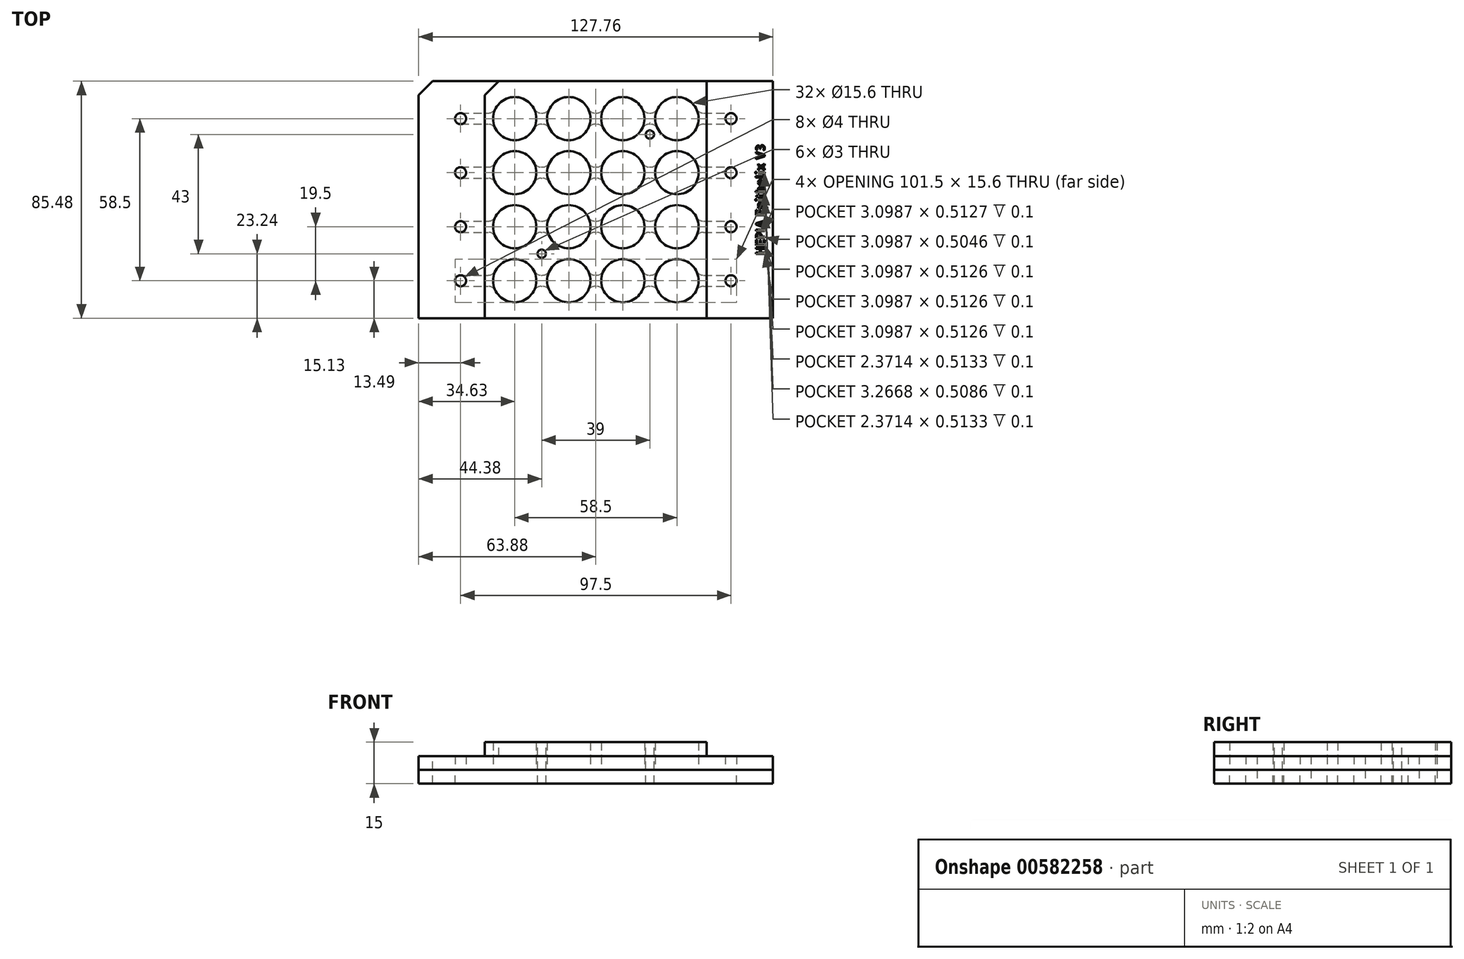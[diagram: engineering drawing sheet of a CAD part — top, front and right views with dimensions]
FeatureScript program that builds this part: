
annotation { "Feature Type Name" : "Feature", "Feature Type Description" : "" }
export const myFeature = defineFeature(function(context is Context, id is Id, definition is map)
    precondition{}
    {
        {
            var Q0;
            Q0=qCreatedBy(makeId("Top.planeOp"),FACE);
            var sketch = newSketch(context, id + "F0", { "sketchPlane" : qUnion([Q0])});
            skLineSegment(sketch, "E0.bottom", {"start": v(63.88, 42.74) * mm, "end": v(-63.88, 42.74) * mm});
            skLineSegment(sketch, "E0.top", {"start": v(63.88, -42.74) * mm, "end": v(-63.88, -42.74) * mm});
            skLineSegment(sketch, "E0.left", {"start": v(63.88, 42.74) * mm, "end": v(63.88, -42.74) * mm});
            skLineSegment(sketch, "E0.right", {"start": v(-63.88, 42.74) * mm, "end": v(-63.88, -42.74) * mm});
            skPoint(sketch, "E0.middle", {"position": v(0, 0) * mm});
            skPoint(sketch, "E1", {"position": v(-48.75, 29.25) * mm});
            skPoint(sketch, "E2.0.1.0", {"position": v(-48.75, 9.75) * mm});
            skPoint(sketch, "E2.1.0.0", {"position": v(-29.25, 29.25) * mm});
            skPoint(sketch, "E2.1.1.0", {"position": v(-29.25, 9.75) * mm});
            skPoint(sketch, "E2.2.0.0", {"position": v(-9.75, 29.25) * mm});
            skPoint(sketch, "E2.2.1.0", {"position": v(-9.75, 9.75) * mm});
            skLineSegment(sketch, "E2.direction1", {"start": v(-48.75, 29.25) * mm, "end": v(-29.25, 29.25) * mm, "construction": true});
            skLineSegment(sketch, "E2.direction2", {"start": v(-48.75, 29.25) * mm, "end": v(-48.75, 9.75) * mm, "construction": true});
            skCircle(sketch, "E3", {"center": v(-48.75, 29.25) * mm, "radius": 2 * mm});
            skCircle(sketch, "E4", {"center": v(-29.25, 29.25) * mm, "radius": 7.8 * mm});
            skCircle(sketch, "E5", {"center": v(-29.25, 9.75) * mm, "radius": 7.8 * mm});
            skCircle(sketch, "E6", {"center": v(-48.75, 9.75) * mm, "radius": 2 * mm});
            skCircle(sketch, "E7", {"center": v(-9.75, 29.25) * mm, "radius": 7.8 * mm});
            skCircle(sketch, "E8", {"center": v(-9.75, 9.75) * mm, "radius": 7.8 * mm});
            skCircle(sketch, "E9.MirrorC", {"center": v(48.75, 29.25) * mm, "radius": 2 * mm});
            skCircle(sketch, "E10.MirrorC", {"center": v(48.75, 9.75) * mm, "radius": 2 * mm});
            skCircle(sketch, "E11.MirrorC", {"center": v(29.25, 9.75) * mm, "radius": 7.8 * mm});
            skCircle(sketch, "E12.MirrorC", {"center": v(29.25, 29.25) * mm, "radius": 7.8 * mm});
            skCircle(sketch, "E13.MirrorC", {"center": v(9.75, 29.25) * mm, "radius": 7.8 * mm});
            skCircle(sketch, "E14.MirrorC", {"center": v(9.75, 9.75) * mm, "radius": 7.8 * mm});
            skCircle(sketch, "E15.MirrorC", {"center": v(-48.75, -29.25) * mm, "radius": 2 * mm});
            skCircle(sketch, "E16.MirrorC", {"center": v(-48.75, -9.75) * mm, "radius": 2 * mm});
            skCircle(sketch, "E17.MirrorC", {"center": v(-29.25, -9.75) * mm, "radius": 7.8 * mm});
            skCircle(sketch, "E18.MirrorC", {"center": v(-29.25, -29.25) * mm, "radius": 7.8 * mm});
            skCircle(sketch, "E19.MirrorC", {"center": v(-9.75, -29.25) * mm, "radius": 7.8 * mm});
            skCircle(sketch, "E20.MirrorC", {"center": v(-9.75, -9.75) * mm, "radius": 7.8 * mm});
            skCircle(sketch, "E21.MirrorC", {"center": v(9.75, -9.75) * mm, "radius": 7.8 * mm});
            skCircle(sketch, "E22.MirrorC", {"center": v(9.75, -29.25) * mm, "radius": 7.8 * mm});
            skCircle(sketch, "E23.MirrorC", {"center": v(29.25, -29.25) * mm, "radius": 7.8 * mm});
            skCircle(sketch, "E24.MirrorC", {"center": v(29.25, -9.75) * mm, "radius": 7.8 * mm});
            skCircle(sketch, "E25.MirrorC", {"center": v(48.75, -9.75) * mm, "radius": 2 * mm});
            skCircle(sketch, "E26.MirrorC", {"center": v(48.75, -29.25) * mm, "radius": 2 * mm});
            skSolve(sketch);
        }
        {
            var Q0;
            Q0 = qSketchRegion(id + "F0", true);
            extrude(context, id + "F1", {"entities" : qUnion([Q0]), "depth" : 5 * mm, "offsetDistance" : 25 * mm});
        }
        {
            var Q0;
            Q0=makeQuery(id+"F1.opExtrude","CAP_FACE",FACE,{"disambiguationData":[OSD([sQuery(id+"F0.wireOp",EDGE,"E0.bottom"),sQuery(id+"F0.wireOp",EDGE,"E0.top"),sQuery(id+"F0.wireOp",EDGE,"E0.left"),sQuery(id+"F0.wireOp",EDGE,"E0.right"),sQuery(id+"F0.wireOp",EDGE,"E3"),sQuery(id+"F0.wireOp",EDGE,"E4"),sQuery(id+"F0.wireOp",EDGE,"E5"),sQuery(id+"F0.wireOp",EDGE,"E6"),sQuery(id+"F0.wireOp",EDGE,"E7"),sQuery(id+"F0.wireOp",EDGE,"E8"),sQuery(id+"F0.wireOp",EDGE,"E9.MirrorC"),sQuery(id+"F0.wireOp",EDGE,"E10.MirrorC"),sQuery(id+"F0.wireOp",EDGE,"E11.MirrorC"),sQuery(id+"F0.wireOp",EDGE,"E12.MirrorC"),sQuery(id+"F0.wireOp",EDGE,"E13.MirrorC"),sQuery(id+"F0.wireOp",EDGE,"E14.MirrorC"),sQuery(id+"F0.wireOp",EDGE,"E15.MirrorC"),sQuery(id+"F0.wireOp",EDGE,"E16.MirrorC"),sQuery(id+"F0.wireOp",EDGE,"E17.MirrorC"),sQuery(id+"F0.wireOp",EDGE,"E18.MirrorC"),sQuery(id+"F0.wireOp",EDGE,"E19.MirrorC"),sQuery(id+"F0.wireOp",EDGE,"E20.MirrorC"),sQuery(id+"F0.wireOp",EDGE,"E21.MirrorC"),sQuery(id+"F0.wireOp",EDGE,"E22.MirrorC"),sQuery(id+"F0.wireOp",EDGE,"E23.MirrorC"),sQuery(id+"F0.wireOp",EDGE,"E24.MirrorC"),sQuery(id+"F0.wireOp",EDGE,"E25.MirrorC"),sQuery(id+"F0.wireOp",EDGE,"E26.MirrorC")])],"isStart":false});
            var sketch = newSketch(context, id + "F2", { "sketchPlane" : qUnion([Q0])});
            skLineSegment(sketch, "E27.bottom", {"start": v(40, 42.74) * mm, "end": v(-40, 42.74) * mm});
            skLineSegment(sketch, "E27.top", {"start": v(40, -42.74) * mm, "end": v(-40, -42.74) * mm});
            skLineSegment(sketch, "E27.left", {"start": v(40, 42.74) * mm, "end": v(40, -42.74) * mm});
            skLineSegment(sketch, "E27.right", {"start": v(-40, 42.74) * mm, "end": v(-40, -42.74) * mm});
            skPoint(sketch, "E27.middle", {"position": v(0, 0) * mm});
            skCircle(sketch, "E28.0", {"center": v(-29.25, -29.25) * mm, "radius": 7.8 * mm});
            skCircle(sketch, "E28.1", {"center": v(-29.25, -9.75) * mm, "radius": 7.8 * mm});
            skCircle(sketch, "E28.2", {"center": v(-29.25, 9.75) * mm, "radius": 7.8 * mm});
            skCircle(sketch, "E28.3", {"center": v(-9.75, -29.25) * mm, "radius": 7.8 * mm});
            skCircle(sketch, "E28.4", {"center": v(9.75, -29.25) * mm, "radius": 7.8 * mm});
            skCircle(sketch, "E28.5", {"center": v(9.75, -9.75) * mm, "radius": 7.8 * mm});
            skCircle(sketch, "E28.6", {"center": v(9.75, 9.75) * mm, "radius": 7.8 * mm});
            skCircle(sketch, "E28.7", {"center": v(9.75, 29.25) * mm, "radius": 7.8 * mm});
            skCircle(sketch, "E28.8", {"center": v(29.25, 29.25) * mm, "radius": 7.8 * mm});
            skCircle(sketch, "E28.9", {"center": v(29.25, 9.75) * mm, "radius": 7.8 * mm});
            skCircle(sketch, "E28.10", {"center": v(29.25, -9.75) * mm, "radius": 7.8 * mm});
            skCircle(sketch, "E28.11", {"center": v(29.25, -29.25) * mm, "radius": 7.8 * mm});
            skCircle(sketch, "E28.12", {"center": v(-29.25, 29.25) * mm, "radius": 7.8 * mm});
            skCircle(sketch, "E28.13", {"center": v(-9.75, -9.75) * mm, "radius": 7.8 * mm});
            skCircle(sketch, "E28.14", {"center": v(-9.75, 9.75) * mm, "radius": 7.8 * mm});
            skCircle(sketch, "E28.15", {"center": v(-9.75, 29.25) * mm, "radius": 7.8 * mm});
            skSolve(sketch);
        }
        {
            var Q0;
            Q0 = qSketchRegion(id + "F2", true);
            extrude(context, id + "F3", {"entities" : qUnion([Q0]), "depth" : 5 * mm, "offsetDistance" : 25 * mm});
        }
        {
            var Q0;
            Q0=makeQuery(id+"F1.opExtrude","CAP_FACE",FACE,{"disambiguationData":[OSD([sQuery(id+"F0.wireOp",EDGE,"E0.bottom"),sQuery(id+"F0.wireOp",EDGE,"E0.top"),sQuery(id+"F0.wireOp",EDGE,"E0.left"),sQuery(id+"F0.wireOp",EDGE,"E0.right"),sQuery(id+"F0.wireOp",EDGE,"E3"),sQuery(id+"F0.wireOp",EDGE,"E4"),sQuery(id+"F0.wireOp",EDGE,"E5"),sQuery(id+"F0.wireOp",EDGE,"E6"),sQuery(id+"F0.wireOp",EDGE,"E7"),sQuery(id+"F0.wireOp",EDGE,"E8"),sQuery(id+"F0.wireOp",EDGE,"E9.MirrorC"),sQuery(id+"F0.wireOp",EDGE,"E10.MirrorC"),sQuery(id+"F0.wireOp",EDGE,"E11.MirrorC"),sQuery(id+"F0.wireOp",EDGE,"E12.MirrorC"),sQuery(id+"F0.wireOp",EDGE,"E13.MirrorC"),sQuery(id+"F0.wireOp",EDGE,"E14.MirrorC"),sQuery(id+"F0.wireOp",EDGE,"E15.MirrorC"),sQuery(id+"F0.wireOp",EDGE,"E16.MirrorC"),sQuery(id+"F0.wireOp",EDGE,"E17.MirrorC"),sQuery(id+"F0.wireOp",EDGE,"E18.MirrorC"),sQuery(id+"F0.wireOp",EDGE,"E19.MirrorC"),sQuery(id+"F0.wireOp",EDGE,"E20.MirrorC"),sQuery(id+"F0.wireOp",EDGE,"E21.MirrorC"),sQuery(id+"F0.wireOp",EDGE,"E22.MirrorC"),sQuery(id+"F0.wireOp",EDGE,"E23.MirrorC"),sQuery(id+"F0.wireOp",EDGE,"E24.MirrorC"),sQuery(id+"F0.wireOp",EDGE,"E25.MirrorC"),sQuery(id+"F0.wireOp",EDGE,"E26.MirrorC")])],"isStart":true});
            var sketch = newSketch(context, id + "F4", { "sketchPlane" : qUnion([Q0])});
            skCircle(sketch, "E29.0", {"center": v(-48.75, 29.25) * mm, "radius": 2 * mm});
            skCircle(sketch, "E29.1", {"center": v(-29.25, 29.25) * mm, "radius": 7.8 * mm});
            skCircle(sketch, "E29.2", {"center": v(-9.75, 29.25) * mm, "radius": 7.8 * mm});
            skCircle(sketch, "E29.3", {"center": v(9.75, 29.25) * mm, "radius": 7.8 * mm});
            skCircle(sketch, "E29.4", {"center": v(29.25, 29.25) * mm, "radius": 7.8 * mm});
            skCircle(sketch, "E29.5", {"center": v(48.75, 29.25) * mm, "radius": 2 * mm});
            skCircle(sketch, "E29.6", {"center": v(48.75, 9.75) * mm, "radius": 2 * mm});
            skCircle(sketch, "E29.7", {"center": v(29.25, 9.75) * mm, "radius": 7.8 * mm});
            skCircle(sketch, "E29.8", {"center": v(9.75, 9.75) * mm, "radius": 7.8 * mm});
            skCircle(sketch, "E29.9", {"center": v(-9.75, 9.75) * mm, "radius": 7.8 * mm});
            skCircle(sketch, "E29.10", {"center": v(-29.25, 9.75) * mm, "radius": 7.8 * mm});
            skCircle(sketch, "E29.11", {"center": v(-48.75, 9.75) * mm, "radius": 2 * mm});
            skCircle(sketch, "E29.12", {"center": v(-48.75, -9.75) * mm, "radius": 2 * mm});
            skCircle(sketch, "E29.13", {"center": v(-29.25, -9.75) * mm, "radius": 7.8 * mm});
            skCircle(sketch, "E29.14", {"center": v(-9.75, -9.75) * mm, "radius": 7.8 * mm});
            skCircle(sketch, "E29.15", {"center": v(9.75, -9.75) * mm, "radius": 7.8 * mm});
            skCircle(sketch, "E29.16", {"center": v(29.25, -9.75) * mm, "radius": 7.8 * mm});
            skCircle(sketch, "E29.17", {"center": v(48.75, -9.75) * mm, "radius": 2 * mm});
            skCircle(sketch, "E29.18", {"center": v(48.75, -29.25) * mm, "radius": 2 * mm});
            skCircle(sketch, "E29.19", {"center": v(29.25, -29.25) * mm, "radius": 7.8 * mm});
            skCircle(sketch, "E29.20", {"center": v(9.75, -29.25) * mm, "radius": 7.8 * mm});
            skCircle(sketch, "E29.21", {"center": v(-9.75, -29.25) * mm, "radius": 7.8 * mm});
            skCircle(sketch, "E29.22", {"center": v(-29.25, -29.25) * mm, "radius": 7.8 * mm});
            skCircle(sketch, "E29.23", {"center": v(-48.75, -29.25) * mm, "radius": 2 * mm});
            skLineSegment(sketch, "E30.bottom", {"start": v(-48.75, 27.25) * mm, "end": v(48.75, 27.25) * mm});
            skLineSegment(sketch, "E30.top", {"start": v(-48.75, 31.25) * mm, "end": v(48.75, 31.25) * mm});
            skLineSegment(sketch, "E30.left", {"start": v(-48.75, 27.25) * mm, "end": v(-48.75, 31.25) * mm});
            skLineSegment(sketch, "E30.right", {"start": v(48.75, 27.25) * mm, "end": v(48.75, 31.25) * mm});
            skLineSegment(sketch, "E31.bottom", {"start": v(-48.75, 7.75) * mm, "end": v(48.75, 7.75) * mm});
            skLineSegment(sketch, "E31.top", {"start": v(-48.75, 11.75) * mm, "end": v(48.75, 11.75) * mm});
            skLineSegment(sketch, "E31.left", {"start": v(-48.75, 7.75) * mm, "end": v(-48.75, 11.75) * mm});
            skLineSegment(sketch, "E31.right", {"start": v(48.75, 7.75) * mm, "end": v(48.75, 11.75) * mm});
            skLineSegment(sketch, "E32.bottom", {"start": v(-48.75, -11.75) * mm, "end": v(48.75, -11.75) * mm});
            skLineSegment(sketch, "E32.top", {"start": v(-48.75, -7.75) * mm, "end": v(48.75, -7.75) * mm});
            skLineSegment(sketch, "E32.left", {"start": v(-48.75, -11.75) * mm, "end": v(-48.75, -7.75) * mm});
            skLineSegment(sketch, "E32.right", {"start": v(48.75, -11.75) * mm, "end": v(48.75, -7.75) * mm});
            skLineSegment(sketch, "E33.bottom", {"start": v(-48.75, -31.25) * mm, "end": v(48.75, -31.25) * mm});
            skLineSegment(sketch, "E33.top", {"start": v(-48.75, -27.25) * mm, "end": v(48.75, -27.25) * mm});
            skLineSegment(sketch, "E33.left", {"start": v(-48.75, -31.25) * mm, "end": v(-48.75, -27.25) * mm});
            skLineSegment(sketch, "E33.right", {"start": v(48.75, -31.25) * mm, "end": v(48.75, -27.25) * mm});
            skSolve(sketch);
        }
        {
            var Q0;
            Q0=makeQuery(id+"F4.imprint","IMPRINT",FACE,{"disambiguationData":[TD([[makeQuery(id+"F4.imprint","IMPRINT",EDGE,{"derivedFrom":makeQuery(id+"F1.opExtrude","CAP_EDGE",EDGE,{"disambiguationData":[OSD([sQuery(id+"F0.wireOp",EDGE,"E0.bottom")])],"isStart":true})}),-1.0]])]});
            extrude(context, id + "F5", {"entities" : qUnion([Q0]), "depth" : 5 * mm, "offsetDistance" : 25 * mm});
        }
        {
            var Q0;
            {var subQ0=sQuery(id+"F4.wireOp",EDGE,"E30.top");var subQ1=sQuery(id+"F4.wireOp",EDGE,"E29.1");Q0=makeQuery(id+"F5.opExtrude","SWEPT_EDGE",EDGE,{"disambiguationData":[OSD([subQ1,subQ0]),TDD([makeQuery(id+"F4.imprint","INTERSECT",VERTEX,{"disambiguationData":[OD(0.0)],"derivedFrom":[subQ1,subQ0]})])]});}
            var Q1;
            {var subQ0=sQuery(id+"F4.wireOp",EDGE,"E30.bottom");var subQ1=sQuery(id+"F4.wireOp",EDGE,"E29.1");Q1=makeQuery(id+"F5.opExtrude","SWEPT_EDGE",EDGE,{"disambiguationData":[OSD([subQ1,subQ0]),TDD([makeQuery(id+"F4.imprint","INTERSECT",VERTEX,{"disambiguationData":[OD(0.0)],"derivedFrom":[subQ1,subQ0]})])]});}
            var Q2;
            {var subQ0=sQuery(id+"F4.wireOp",EDGE,"E30.top");var subQ1=sQuery(id+"F4.wireOp",EDGE,"E29.1");Q2=makeQuery(id+"F5.opExtrude","SWEPT_EDGE",EDGE,{"disambiguationData":[OSD([subQ1,subQ0]),TDD([makeQuery(id+"F4.imprint","INTERSECT",VERTEX,{"disambiguationData":[OD(1.0)],"derivedFrom":[subQ1,subQ0]})])]});}
            var Q3;
            {var subQ0=sQuery(id+"F4.wireOp",EDGE,"E30.top");var subQ1=sQuery(id+"F4.wireOp",EDGE,"E29.2");Q3=makeQuery(id+"F5.opExtrude","SWEPT_EDGE",EDGE,{"disambiguationData":[OSD([subQ1,subQ0]),TDD([makeQuery(id+"F4.imprint","INTERSECT",VERTEX,{"disambiguationData":[OD(1.0)],"derivedFrom":[subQ1,subQ0]})])]});}
            var Q4;
            {var subQ0=sQuery(id+"F4.wireOp",EDGE,"E30.top");var subQ1=sQuery(id+"F4.wireOp",EDGE,"E29.3");Q4=makeQuery(id+"F5.opExtrude","SWEPT_EDGE",EDGE,{"disambiguationData":[OSD([subQ1,subQ0]),TDD([makeQuery(id+"F4.imprint","INTERSECT",VERTEX,{"disambiguationData":[OD(1.0)],"derivedFrom":[subQ1,subQ0]})])]});}
            var Q5;
            {var subQ0=sQuery(id+"F4.wireOp",EDGE,"E30.top");var subQ1=sQuery(id+"F4.wireOp",EDGE,"E29.2");Q5=makeQuery(id+"F5.opExtrude","SWEPT_EDGE",EDGE,{"disambiguationData":[OSD([subQ1,subQ0]),TDD([makeQuery(id+"F4.imprint","INTERSECT",VERTEX,{"disambiguationData":[OD(0.0)],"derivedFrom":[subQ1,subQ0]})])]});}
            var Q6;
            {var subQ0=sQuery(id+"F4.wireOp",EDGE,"E31.top");var subQ1=sQuery(id+"F4.wireOp",EDGE,"E29.10");Q6=makeQuery(id+"F5.opExtrude","SWEPT_EDGE",EDGE,{"disambiguationData":[OSD([subQ1,subQ0]),TDD([makeQuery(id+"F4.imprint","INTERSECT",VERTEX,{"disambiguationData":[OD(0.0)],"derivedFrom":[subQ1,subQ0]})])]});}
            var Q7;
            {var subQ0=sQuery(id+"F4.wireOp",EDGE,"E30.top");var subQ1=sQuery(id+"F4.wireOp",EDGE,"E29.3");Q7=makeQuery(id+"F5.opExtrude","SWEPT_EDGE",EDGE,{"disambiguationData":[OSD([subQ1,subQ0]),TDD([makeQuery(id+"F4.imprint","INTERSECT",VERTEX,{"disambiguationData":[OD(0.0)],"derivedFrom":[subQ1,subQ0]})])]});}
            var Q8;
            {var subQ0=sQuery(id+"F4.wireOp",EDGE,"E30.top");var subQ1=sQuery(id+"F4.wireOp",EDGE,"E29.4");Q8=makeQuery(id+"F5.opExtrude","SWEPT_EDGE",EDGE,{"disambiguationData":[OSD([subQ1,subQ0]),TDD([makeQuery(id+"F4.imprint","INTERSECT",VERTEX,{"disambiguationData":[OD(1.0)],"derivedFrom":[subQ1,subQ0]})])]});}
            var Q9;
            {var subQ0=sQuery(id+"F4.wireOp",EDGE,"E30.top");var subQ1=sQuery(id+"F4.wireOp",EDGE,"E29.4");Q9=makeQuery(id+"F5.opExtrude","SWEPT_EDGE",EDGE,{"disambiguationData":[OSD([subQ1,subQ0]),TDD([makeQuery(id+"F4.imprint","INTERSECT",VERTEX,{"disambiguationData":[OD(0.0)],"derivedFrom":[subQ1,subQ0]})])]});}
            var Q10;
            {var subQ0=sQuery(id+"F4.wireOp",EDGE,"E30.bottom");var subQ1=sQuery(id+"F4.wireOp",EDGE,"E29.4");Q10=makeQuery(id+"F5.opExtrude","SWEPT_EDGE",EDGE,{"disambiguationData":[OSD([subQ1,subQ0]),TDD([makeQuery(id+"F4.imprint","INTERSECT",VERTEX,{"disambiguationData":[OD(1.0)],"derivedFrom":[subQ1,subQ0]})])]});}
            var Q11;
            {var subQ0=sQuery(id+"F4.wireOp",EDGE,"E31.top");var subQ1=sQuery(id+"F4.wireOp",EDGE,"E29.10");Q11=makeQuery(id+"F5.opExtrude","SWEPT_EDGE",EDGE,{"disambiguationData":[OSD([subQ1,subQ0]),TDD([makeQuery(id+"F4.imprint","INTERSECT",VERTEX,{"disambiguationData":[OD(1.0)],"derivedFrom":[subQ1,subQ0]})])]});}
            var Q12;
            {var subQ0=sQuery(id+"F4.wireOp",EDGE,"E31.top");var subQ1=sQuery(id+"F4.wireOp",EDGE,"E29.9");Q12=makeQuery(id+"F5.opExtrude","SWEPT_EDGE",EDGE,{"disambiguationData":[OSD([subQ1,subQ0]),TDD([makeQuery(id+"F4.imprint","INTERSECT",VERTEX,{"disambiguationData":[OD(0.0)],"derivedFrom":[subQ1,subQ0]})])]});}
            var Q13;
            {var subQ0=sQuery(id+"F4.wireOp",EDGE,"E31.top");var subQ1=sQuery(id+"F4.wireOp",EDGE,"E29.9");Q13=makeQuery(id+"F5.opExtrude","SWEPT_EDGE",EDGE,{"disambiguationData":[OSD([subQ1,subQ0]),TDD([makeQuery(id+"F4.imprint","INTERSECT",VERTEX,{"disambiguationData":[OD(1.0)],"derivedFrom":[subQ1,subQ0]})])]});}
            var Q14;
            {var subQ0=sQuery(id+"F4.wireOp",EDGE,"E31.top");var subQ1=sQuery(id+"F4.wireOp",EDGE,"E29.8");Q14=makeQuery(id+"F5.opExtrude","SWEPT_EDGE",EDGE,{"disambiguationData":[OSD([subQ1,subQ0]),TDD([makeQuery(id+"F4.imprint","INTERSECT",VERTEX,{"disambiguationData":[OD(1.0)],"derivedFrom":[subQ1,subQ0]})])]});}
            var Q15;
            {var subQ0=sQuery(id+"F4.wireOp",EDGE,"E31.top");var subQ1=sQuery(id+"F4.wireOp",EDGE,"E29.8");Q15=makeQuery(id+"F5.opExtrude","SWEPT_EDGE",EDGE,{"disambiguationData":[OSD([subQ1,subQ0]),TDD([makeQuery(id+"F4.imprint","INTERSECT",VERTEX,{"disambiguationData":[OD(0.0)],"derivedFrom":[subQ1,subQ0]})])]});}
            var Q16;
            {var subQ0=sQuery(id+"F4.wireOp",EDGE,"E31.top");var subQ1=sQuery(id+"F4.wireOp",EDGE,"E29.7");Q16=makeQuery(id+"F5.opExtrude","SWEPT_EDGE",EDGE,{"disambiguationData":[OSD([subQ1,subQ0]),TDD([makeQuery(id+"F4.imprint","INTERSECT",VERTEX,{"disambiguationData":[OD(1.0)],"derivedFrom":[subQ1,subQ0]})])]});}
            var Q17;
            {var subQ0=sQuery(id+"F4.wireOp",EDGE,"E31.top");var subQ1=sQuery(id+"F4.wireOp",EDGE,"E29.7");Q17=makeQuery(id+"F5.opExtrude","SWEPT_EDGE",EDGE,{"disambiguationData":[OSD([subQ1,subQ0]),TDD([makeQuery(id+"F4.imprint","INTERSECT",VERTEX,{"disambiguationData":[OD(0.0)],"derivedFrom":[subQ1,subQ0]})])]});}
            var Q18;
            {var subQ0=sQuery(id+"F4.wireOp",EDGE,"E32.top");var subQ1=sQuery(id+"F4.wireOp",EDGE,"E29.16");Q18=makeQuery(id+"F5.opExtrude","SWEPT_EDGE",EDGE,{"disambiguationData":[OSD([subQ1,subQ0]),TDD([makeQuery(id+"F4.imprint","INTERSECT",VERTEX,{"disambiguationData":[OD(0.0)],"derivedFrom":[subQ1,subQ0]})])]});}
            var Q19;
            {var subQ0=sQuery(id+"F4.wireOp",EDGE,"E33.top");var subQ1=sQuery(id+"F4.wireOp",EDGE,"E29.19");Q19=makeQuery(id+"F5.opExtrude","SWEPT_EDGE",EDGE,{"disambiguationData":[OSD([subQ1,subQ0]),TDD([makeQuery(id+"F4.imprint","INTERSECT",VERTEX,{"disambiguationData":[OD(0.0)],"derivedFrom":[subQ1,subQ0]})])]});}
            var Q20;
            {var subQ0=sQuery(id+"F4.wireOp",EDGE,"E33.top");var subQ1=sQuery(id+"F4.wireOp",EDGE,"E29.19");Q20=makeQuery(id+"F5.opExtrude","SWEPT_EDGE",EDGE,{"disambiguationData":[OSD([subQ1,subQ0]),TDD([makeQuery(id+"F4.imprint","INTERSECT",VERTEX,{"disambiguationData":[OD(1.0)],"derivedFrom":[subQ1,subQ0]})])]});}
            var Q21;
            {var subQ0=sQuery(id+"F4.wireOp",EDGE,"E32.top");var subQ1=sQuery(id+"F4.wireOp",EDGE,"E29.16");Q21=makeQuery(id+"F5.opExtrude","SWEPT_EDGE",EDGE,{"disambiguationData":[OSD([subQ1,subQ0]),TDD([makeQuery(id+"F4.imprint","INTERSECT",VERTEX,{"disambiguationData":[OD(1.0)],"derivedFrom":[subQ1,subQ0]})])]});}
            var Q22;
            {var subQ0=sQuery(id+"F4.wireOp",EDGE,"E32.top");var subQ1=sQuery(id+"F4.wireOp",EDGE,"E29.15");Q22=makeQuery(id+"F5.opExtrude","SWEPT_EDGE",EDGE,{"disambiguationData":[OSD([subQ1,subQ0]),TDD([makeQuery(id+"F4.imprint","INTERSECT",VERTEX,{"disambiguationData":[OD(0.0)],"derivedFrom":[subQ1,subQ0]})])]});}
            var Q23;
            {var subQ0=sQuery(id+"F4.wireOp",EDGE,"E32.bottom");var subQ1=sQuery(id+"F4.wireOp",EDGE,"E29.16");Q23=makeQuery(id+"F5.opExtrude","SWEPT_EDGE",EDGE,{"disambiguationData":[OSD([subQ1,subQ0]),TDD([makeQuery(id+"F4.imprint","INTERSECT",VERTEX,{"disambiguationData":[OD(1.0)],"derivedFrom":[subQ1,subQ0]})])]});}
            var Q24;
            {var subQ0=sQuery(id+"F4.wireOp",EDGE,"E31.bottom");var subQ1=sQuery(id+"F4.wireOp",EDGE,"E29.7");Q24=makeQuery(id+"F5.opExtrude","SWEPT_EDGE",EDGE,{"disambiguationData":[OSD([subQ1,subQ0]),TDD([makeQuery(id+"F4.imprint","INTERSECT",VERTEX,{"disambiguationData":[OD(1.0)],"derivedFrom":[subQ1,subQ0]})])]});}
            var Q25;
            {var subQ0=sQuery(id+"F4.wireOp",EDGE,"E30.bottom");var subQ1=sQuery(id+"F4.wireOp",EDGE,"E29.3");Q25=makeQuery(id+"F5.opExtrude","SWEPT_EDGE",EDGE,{"disambiguationData":[OSD([subQ1,subQ0]),TDD([makeQuery(id+"F4.imprint","INTERSECT",VERTEX,{"disambiguationData":[OD(1.0)],"derivedFrom":[subQ1,subQ0]})])]});}
            var Q26;
            {var subQ0=sQuery(id+"F4.wireOp",EDGE,"E30.bottom");var subQ1=sQuery(id+"F4.wireOp",EDGE,"E29.2");Q26=makeQuery(id+"F5.opExtrude","SWEPT_EDGE",EDGE,{"disambiguationData":[OSD([subQ1,subQ0]),TDD([makeQuery(id+"F4.imprint","INTERSECT",VERTEX,{"disambiguationData":[OD(0.0)],"derivedFrom":[subQ1,subQ0]})])]});}
            var Q27;
            {var subQ0=sQuery(id+"F4.wireOp",EDGE,"E31.bottom");var subQ1=sQuery(id+"F4.wireOp",EDGE,"E29.9");Q27=makeQuery(id+"F5.opExtrude","SWEPT_EDGE",EDGE,{"disambiguationData":[OSD([subQ1,subQ0]),TDD([makeQuery(id+"F4.imprint","INTERSECT",VERTEX,{"disambiguationData":[OD(0.0)],"derivedFrom":[subQ1,subQ0]})])]});}
            var Q28;
            {var subQ0=sQuery(id+"F4.wireOp",EDGE,"E31.bottom");var subQ1=sQuery(id+"F4.wireOp",EDGE,"E29.8");Q28=makeQuery(id+"F5.opExtrude","SWEPT_EDGE",EDGE,{"disambiguationData":[OSD([subQ1,subQ0]),TDD([makeQuery(id+"F4.imprint","INTERSECT",VERTEX,{"disambiguationData":[OD(1.0)],"derivedFrom":[subQ1,subQ0]})])]});}
            var Q29;
            {var subQ0=sQuery(id+"F4.wireOp",EDGE,"E32.top");var subQ1=sQuery(id+"F4.wireOp",EDGE,"E29.13");Q29=makeQuery(id+"F5.opExtrude","SWEPT_EDGE",EDGE,{"disambiguationData":[OSD([subQ1,subQ0]),TDD([makeQuery(id+"F4.imprint","INTERSECT",VERTEX,{"disambiguationData":[OD(0.0)],"derivedFrom":[subQ1,subQ0]})])]});}
            var Q30;
            {var subQ0=sQuery(id+"F4.wireOp",EDGE,"E32.top");var subQ1=sQuery(id+"F4.wireOp",EDGE,"E29.13");Q30=makeQuery(id+"F5.opExtrude","SWEPT_EDGE",EDGE,{"disambiguationData":[OSD([subQ1,subQ0]),TDD([makeQuery(id+"F4.imprint","INTERSECT",VERTEX,{"disambiguationData":[OD(1.0)],"derivedFrom":[subQ1,subQ0]})])]});}
            var Q31;
            {var subQ0=sQuery(id+"F4.wireOp",EDGE,"E32.bottom");var subQ1=sQuery(id+"F4.wireOp",EDGE,"E29.13");Q31=makeQuery(id+"F5.opExtrude","SWEPT_EDGE",EDGE,{"disambiguationData":[OSD([subQ1,subQ0]),TDD([makeQuery(id+"F4.imprint","INTERSECT",VERTEX,{"disambiguationData":[OD(0.0)],"derivedFrom":[subQ1,subQ0]})])]});}
            var Q32;
            {var subQ0=sQuery(id+"F4.wireOp",EDGE,"E32.top");var subQ1=sQuery(id+"F4.wireOp",EDGE,"E29.14");Q32=makeQuery(id+"F5.opExtrude","SWEPT_EDGE",EDGE,{"disambiguationData":[OSD([subQ1,subQ0]),TDD([makeQuery(id+"F4.imprint","INTERSECT",VERTEX,{"disambiguationData":[OD(0.0)],"derivedFrom":[subQ1,subQ0]})])]});}
            var Q33;
            {var subQ0=sQuery(id+"F4.wireOp",EDGE,"E32.bottom");var subQ1=sQuery(id+"F4.wireOp",EDGE,"E29.14");Q33=makeQuery(id+"F5.opExtrude","SWEPT_EDGE",EDGE,{"disambiguationData":[OSD([subQ1,subQ0]),TDD([makeQuery(id+"F4.imprint","INTERSECT",VERTEX,{"disambiguationData":[OD(0.0)],"derivedFrom":[subQ1,subQ0]})])]});}
            var Q34;
            {var subQ0=sQuery(id+"F4.wireOp",EDGE,"E32.top");var subQ1=sQuery(id+"F4.wireOp",EDGE,"E29.14");Q34=makeQuery(id+"F5.opExtrude","SWEPT_EDGE",EDGE,{"disambiguationData":[OSD([subQ1,subQ0]),TDD([makeQuery(id+"F4.imprint","INTERSECT",VERTEX,{"disambiguationData":[OD(1.0)],"derivedFrom":[subQ1,subQ0]})])]});}
            var Q35;
            {var subQ0=sQuery(id+"F4.wireOp",EDGE,"E32.top");var subQ1=sQuery(id+"F4.wireOp",EDGE,"E29.15");Q35=makeQuery(id+"F5.opExtrude","SWEPT_EDGE",EDGE,{"disambiguationData":[OSD([subQ1,subQ0]),TDD([makeQuery(id+"F4.imprint","INTERSECT",VERTEX,{"disambiguationData":[OD(1.0)],"derivedFrom":[subQ1,subQ0]})])]});}
            var Q36;
            {var subQ0=sQuery(id+"F4.wireOp",EDGE,"E32.bottom");var subQ1=sQuery(id+"F4.wireOp",EDGE,"E29.15");Q36=makeQuery(id+"F5.opExtrude","SWEPT_EDGE",EDGE,{"disambiguationData":[OSD([subQ1,subQ0]),TDD([makeQuery(id+"F4.imprint","INTERSECT",VERTEX,{"disambiguationData":[OD(1.0)],"derivedFrom":[subQ1,subQ0]})])]});}
            var Q37;
            {var subQ0=sQuery(id+"F4.wireOp",EDGE,"E33.top");var subQ1=sQuery(id+"F4.wireOp",EDGE,"E29.22");Q37=makeQuery(id+"F5.opExtrude","SWEPT_EDGE",EDGE,{"disambiguationData":[OSD([subQ1,subQ0]),TDD([makeQuery(id+"F4.imprint","INTERSECT",VERTEX,{"disambiguationData":[OD(0.0)],"derivedFrom":[subQ1,subQ0]})])]});}
            var Q38;
            {var subQ0=sQuery(id+"F4.wireOp",EDGE,"E33.bottom");var subQ1=sQuery(id+"F4.wireOp",EDGE,"E29.22");Q38=makeQuery(id+"F5.opExtrude","SWEPT_EDGE",EDGE,{"disambiguationData":[OSD([subQ1,subQ0]),TDD([makeQuery(id+"F4.imprint","INTERSECT",VERTEX,{"disambiguationData":[OD(0.0)],"derivedFrom":[subQ1,subQ0]})])]});}
            var Q39;
            {var subQ0=sQuery(id+"F4.wireOp",EDGE,"E33.top");var subQ1=sQuery(id+"F4.wireOp",EDGE,"E29.22");Q39=makeQuery(id+"F5.opExtrude","SWEPT_EDGE",EDGE,{"disambiguationData":[OSD([subQ1,subQ0]),TDD([makeQuery(id+"F4.imprint","INTERSECT",VERTEX,{"disambiguationData":[OD(1.0)],"derivedFrom":[subQ1,subQ0]})])]});}
            var Q40;
            {var subQ0=sQuery(id+"F4.wireOp",EDGE,"E33.top");var subQ1=sQuery(id+"F4.wireOp",EDGE,"E29.21");Q40=makeQuery(id+"F5.opExtrude","SWEPT_EDGE",EDGE,{"disambiguationData":[OSD([subQ1,subQ0]),TDD([makeQuery(id+"F4.imprint","INTERSECT",VERTEX,{"disambiguationData":[OD(0.0)],"derivedFrom":[subQ1,subQ0]})])]});}
            var Q41;
            {var subQ0=sQuery(id+"F4.wireOp",EDGE,"E33.bottom");var subQ1=sQuery(id+"F4.wireOp",EDGE,"E29.21");Q41=makeQuery(id+"F5.opExtrude","SWEPT_EDGE",EDGE,{"disambiguationData":[OSD([subQ1,subQ0]),TDD([makeQuery(id+"F4.imprint","INTERSECT",VERTEX,{"disambiguationData":[OD(0.0)],"derivedFrom":[subQ1,subQ0]})])]});}
            var Q42;
            {var subQ0=sQuery(id+"F4.wireOp",EDGE,"E33.top");var subQ1=sQuery(id+"F4.wireOp",EDGE,"E29.21");Q42=makeQuery(id+"F5.opExtrude","SWEPT_EDGE",EDGE,{"disambiguationData":[OSD([subQ1,subQ0]),TDD([makeQuery(id+"F4.imprint","INTERSECT",VERTEX,{"disambiguationData":[OD(1.0)],"derivedFrom":[subQ1,subQ0]})])]});}
            var Q43;
            {var subQ0=sQuery(id+"F4.wireOp",EDGE,"E33.top");var subQ1=sQuery(id+"F4.wireOp",EDGE,"E29.20");Q43=makeQuery(id+"F5.opExtrude","SWEPT_EDGE",EDGE,{"disambiguationData":[OSD([subQ1,subQ0]),TDD([makeQuery(id+"F4.imprint","INTERSECT",VERTEX,{"disambiguationData":[OD(1.0)],"derivedFrom":[subQ1,subQ0]})])]});}
            var Q44;
            {var subQ0=sQuery(id+"F4.wireOp",EDGE,"E33.bottom");var subQ1=sQuery(id+"F4.wireOp",EDGE,"E29.20");Q44=makeQuery(id+"F5.opExtrude","SWEPT_EDGE",EDGE,{"disambiguationData":[OSD([subQ1,subQ0]),TDD([makeQuery(id+"F4.imprint","INTERSECT",VERTEX,{"disambiguationData":[OD(1.0)],"derivedFrom":[subQ1,subQ0]})])]});}
            var Q45;
            {var subQ0=sQuery(id+"F4.wireOp",EDGE,"E33.top");var subQ1=sQuery(id+"F4.wireOp",EDGE,"E29.20");Q45=makeQuery(id+"F5.opExtrude","SWEPT_EDGE",EDGE,{"disambiguationData":[OSD([subQ1,subQ0]),TDD([makeQuery(id+"F4.imprint","INTERSECT",VERTEX,{"disambiguationData":[OD(0.0)],"derivedFrom":[subQ1,subQ0]})])]});}
            var Q46;
            {var subQ0=sQuery(id+"F4.wireOp",EDGE,"E33.bottom");var subQ1=sQuery(id+"F4.wireOp",EDGE,"E29.19");Q46=makeQuery(id+"F5.opExtrude","SWEPT_EDGE",EDGE,{"disambiguationData":[OSD([subQ1,subQ0]),TDD([makeQuery(id+"F4.imprint","INTERSECT",VERTEX,{"disambiguationData":[OD(1.0)],"derivedFrom":[subQ1,subQ0]})])]});}
            var Q47;
            {var subQ0=sQuery(id+"F4.wireOp",EDGE,"E30.bottom");var subQ1=sQuery(id+"F4.wireOp",EDGE,"E29.1");Q47=makeQuery(id+"F5.opExtrude","SWEPT_EDGE",EDGE,{"disambiguationData":[OSD([subQ1,subQ0]),TDD([makeQuery(id+"F4.imprint","INTERSECT",VERTEX,{"disambiguationData":[OD(1.0)],"derivedFrom":[subQ1,subQ0]})])]});}
            var Q48;
            {var subQ0=sQuery(id+"F4.wireOp",EDGE,"E30.bottom");var subQ1=sQuery(id+"F4.wireOp",EDGE,"E29.2");Q48=makeQuery(id+"F5.opExtrude","SWEPT_EDGE",EDGE,{"disambiguationData":[OSD([subQ1,subQ0]),TDD([makeQuery(id+"F4.imprint","INTERSECT",VERTEX,{"disambiguationData":[OD(1.0)],"derivedFrom":[subQ1,subQ0]})])]});}
            var Q49;
            {var subQ0=sQuery(id+"F4.wireOp",EDGE,"E30.bottom");var subQ1=sQuery(id+"F4.wireOp",EDGE,"E29.3");Q49=makeQuery(id+"F5.opExtrude","SWEPT_EDGE",EDGE,{"disambiguationData":[OSD([subQ1,subQ0]),TDD([makeQuery(id+"F4.imprint","INTERSECT",VERTEX,{"disambiguationData":[OD(0.0)],"derivedFrom":[subQ1,subQ0]})])]});}
            var Q50;
            {var subQ0=sQuery(id+"F4.wireOp",EDGE,"E30.bottom");var subQ1=sQuery(id+"F4.wireOp",EDGE,"E29.4");Q50=makeQuery(id+"F5.opExtrude","SWEPT_EDGE",EDGE,{"disambiguationData":[OSD([subQ1,subQ0]),TDD([makeQuery(id+"F4.imprint","INTERSECT",VERTEX,{"disambiguationData":[OD(0.0)],"derivedFrom":[subQ1,subQ0]})])]});}
            var Q51;
            {var subQ0=sQuery(id+"F4.wireOp",EDGE,"E31.bottom");var subQ1=sQuery(id+"F4.wireOp",EDGE,"E29.7");Q51=makeQuery(id+"F5.opExtrude","SWEPT_EDGE",EDGE,{"disambiguationData":[OSD([subQ1,subQ0]),TDD([makeQuery(id+"F4.imprint","INTERSECT",VERTEX,{"disambiguationData":[OD(0.0)],"derivedFrom":[subQ1,subQ0]})])]});}
            var Q52;
            {var subQ0=sQuery(id+"F4.wireOp",EDGE,"E32.bottom");var subQ1=sQuery(id+"F4.wireOp",EDGE,"E29.16");Q52=makeQuery(id+"F5.opExtrude","SWEPT_EDGE",EDGE,{"disambiguationData":[OSD([subQ1,subQ0]),TDD([makeQuery(id+"F4.imprint","INTERSECT",VERTEX,{"disambiguationData":[OD(0.0)],"derivedFrom":[subQ1,subQ0]})])]});}
            var Q53;
            {var subQ0=sQuery(id+"F4.wireOp",EDGE,"E33.bottom");var subQ1=sQuery(id+"F4.wireOp",EDGE,"E29.19");Q53=makeQuery(id+"F5.opExtrude","SWEPT_EDGE",EDGE,{"disambiguationData":[OSD([subQ1,subQ0]),TDD([makeQuery(id+"F4.imprint","INTERSECT",VERTEX,{"disambiguationData":[OD(0.0)],"derivedFrom":[subQ1,subQ0]})])]});}
            var Q54;
            {var subQ0=sQuery(id+"F4.wireOp",EDGE,"E33.bottom");var subQ1=sQuery(id+"F4.wireOp",EDGE,"E29.20");Q54=makeQuery(id+"F5.opExtrude","SWEPT_EDGE",EDGE,{"disambiguationData":[OSD([subQ1,subQ0]),TDD([makeQuery(id+"F4.imprint","INTERSECT",VERTEX,{"disambiguationData":[OD(0.0)],"derivedFrom":[subQ1,subQ0]})])]});}
            var Q55;
            {var subQ0=sQuery(id+"F4.wireOp",EDGE,"E32.bottom");var subQ1=sQuery(id+"F4.wireOp",EDGE,"E29.15");Q55=makeQuery(id+"F5.opExtrude","SWEPT_EDGE",EDGE,{"disambiguationData":[OSD([subQ1,subQ0]),TDD([makeQuery(id+"F4.imprint","INTERSECT",VERTEX,{"disambiguationData":[OD(0.0)],"derivedFrom":[subQ1,subQ0]})])]});}
            var Q56;
            {var subQ0=sQuery(id+"F4.wireOp",EDGE,"E31.bottom");var subQ1=sQuery(id+"F4.wireOp",EDGE,"E29.8");Q56=makeQuery(id+"F5.opExtrude","SWEPT_EDGE",EDGE,{"disambiguationData":[OSD([subQ1,subQ0]),TDD([makeQuery(id+"F4.imprint","INTERSECT",VERTEX,{"disambiguationData":[OD(0.0)],"derivedFrom":[subQ1,subQ0]})])]});}
            var Q57;
            {var subQ0=sQuery(id+"F4.wireOp",EDGE,"E31.bottom");var subQ1=sQuery(id+"F4.wireOp",EDGE,"E29.9");Q57=makeQuery(id+"F5.opExtrude","SWEPT_EDGE",EDGE,{"disambiguationData":[OSD([subQ1,subQ0]),TDD([makeQuery(id+"F4.imprint","INTERSECT",VERTEX,{"disambiguationData":[OD(1.0)],"derivedFrom":[subQ1,subQ0]})])]});}
            var Q58;
            {var subQ0=sQuery(id+"F4.wireOp",EDGE,"E32.bottom");var subQ1=sQuery(id+"F4.wireOp",EDGE,"E29.14");Q58=makeQuery(id+"F5.opExtrude","SWEPT_EDGE",EDGE,{"disambiguationData":[OSD([subQ1,subQ0]),TDD([makeQuery(id+"F4.imprint","INTERSECT",VERTEX,{"disambiguationData":[OD(1.0)],"derivedFrom":[subQ1,subQ0]})])]});}
            var Q59;
            {var subQ0=sQuery(id+"F4.wireOp",EDGE,"E33.bottom");var subQ1=sQuery(id+"F4.wireOp",EDGE,"E29.21");Q59=makeQuery(id+"F5.opExtrude","SWEPT_EDGE",EDGE,{"disambiguationData":[OSD([subQ1,subQ0]),TDD([makeQuery(id+"F4.imprint","INTERSECT",VERTEX,{"disambiguationData":[OD(1.0)],"derivedFrom":[subQ1,subQ0]})])]});}
            var Q60;
            {var subQ0=sQuery(id+"F4.wireOp",EDGE,"E33.bottom");var subQ1=sQuery(id+"F4.wireOp",EDGE,"E29.22");Q60=makeQuery(id+"F5.opExtrude","SWEPT_EDGE",EDGE,{"disambiguationData":[OSD([subQ1,subQ0]),TDD([makeQuery(id+"F4.imprint","INTERSECT",VERTEX,{"disambiguationData":[OD(1.0)],"derivedFrom":[subQ1,subQ0]})])]});}
            var Q61;
            {var subQ0=sQuery(id+"F4.wireOp",EDGE,"E32.bottom");var subQ1=sQuery(id+"F4.wireOp",EDGE,"E29.13");Q61=makeQuery(id+"F5.opExtrude","SWEPT_EDGE",EDGE,{"disambiguationData":[OSD([subQ1,subQ0]),TDD([makeQuery(id+"F4.imprint","INTERSECT",VERTEX,{"disambiguationData":[OD(1.0)],"derivedFrom":[subQ1,subQ0]})])]});}
            var Q62;
            {var subQ0=sQuery(id+"F4.wireOp",EDGE,"E31.bottom");var subQ1=sQuery(id+"F4.wireOp",EDGE,"E29.10");Q62=makeQuery(id+"F5.opExtrude","SWEPT_EDGE",EDGE,{"disambiguationData":[OSD([subQ1,subQ0]),TDD([makeQuery(id+"F4.imprint","INTERSECT",VERTEX,{"disambiguationData":[OD(1.0)],"derivedFrom":[subQ1,subQ0]})])]});}
            var Q63;
            {var subQ0=sQuery(id+"F4.wireOp",EDGE,"E31.bottom");var subQ1=sQuery(id+"F4.wireOp",EDGE,"E29.10");Q63=makeQuery(id+"F5.opExtrude","SWEPT_EDGE",EDGE,{"disambiguationData":[OSD([subQ1,subQ0]),TDD([makeQuery(id+"F4.imprint","INTERSECT",VERTEX,{"disambiguationData":[OD(0.0)],"derivedFrom":[subQ1,subQ0]})])]});}
            fillet(context, id + "F6", {"entities" : qUnion([Q0, Q1, Q2, Q3, Q4, Q5, Q6, Q7, Q8, Q9, Q10, Q11, Q12, Q13, Q14, Q15, Q16, Q17, Q18, Q19, Q20, Q21, Q22, Q23, Q24, Q25, Q26, Q27, Q28, Q29, Q30, Q31, Q32, Q33, Q34, Q35, Q36, Q37, Q38, Q39, Q40, Q41, Q42, Q43, Q44, Q45, Q46, Q47, Q48, Q49, Q50, Q51, Q52, Q53, Q54, Q55, Q56, Q57, Q58, Q59, Q60, Q61, Q62, Q63]), "radius" : 3 * mm, "tangentPropagation" : true, "allowEdgeOverflow" : false});
        }
        {
            var Q0;
            Q0=makeQuery(id+"F3.opExtrude","CAP_FACE",FACE,{"disambiguationData":[OSD([sQuery(id+"F2.wireOp",EDGE,"E27.bottom"),sQuery(id+"F2.wireOp",EDGE,"E27.top"),sQuery(id+"F2.wireOp",EDGE,"E27.left"),sQuery(id+"F2.wireOp",EDGE,"E27.right"),sQuery(id+"F2.wireOp",EDGE,"E28.0"),sQuery(id+"F2.wireOp",EDGE,"E28.1"),sQuery(id+"F2.wireOp",EDGE,"E28.2"),sQuery(id+"F2.wireOp",EDGE,"E28.3"),sQuery(id+"F2.wireOp",EDGE,"E28.4"),sQuery(id+"F2.wireOp",EDGE,"E28.5"),sQuery(id+"F2.wireOp",EDGE,"E28.6"),sQuery(id+"F2.wireOp",EDGE,"E28.7"),sQuery(id+"F2.wireOp",EDGE,"E28.8"),sQuery(id+"F2.wireOp",EDGE,"E28.9"),sQuery(id+"F2.wireOp",EDGE,"E28.10"),sQuery(id+"F2.wireOp",EDGE,"E28.11"),sQuery(id+"F2.wireOp",EDGE,"E28.12"),sQuery(id+"F2.wireOp",EDGE,"E28.13"),sQuery(id+"F2.wireOp",EDGE,"E28.14"),sQuery(id+"F2.wireOp",EDGE,"E28.15")])],"isStart":false});
            var sketch = newSketch(context, id + "F7", { "sketchPlane" : qUnion([Q0])});
            skCircle(sketch, "E34", {"center": v(-19.5, -19.5) * mm, "radius": 1.5 * mm});
            skCircle(sketch, "E35", {"center": v(19.5, 23.5) * mm, "radius": 1.5 * mm});
            skPoint(sketch, "E36", {"position": v(-29.25, -29.25) * mm});
            skPoint(sketch, "E37", {"position": v(-9.75, -9.75) * mm});
            skLineSegment(sketch, "E38", {"start": v(29.25, 29.25) * mm, "end": v(9.75, 9.75) * mm, "construction": true});
            skPoint(sketch, "E39", {"position": v(19.5, 19.5) * mm});
            skSolve(sketch);
        }
        {
            var Q0;
            Q0 = qSketchRegion(id + "F7", true);
            extrude(context, id + "F8", {"entities" : qUnion([Q0]), "operationType" : NewBodyOperationType.REMOVE, "endBound" : BoundingType.THROUGH_ALL, "oppositeDirection" : true, "depth" : 25 * mm, "offsetDistance" : 25 * mm});
        }
        {
            var Q0;
            Q0=makeQuery(id+"F3.opExtrude","SWEPT_EDGE",EDGE,{"disambiguationData":[OSD([sQuery(id+"F0.wireOp",EDGE,"E0.bottom"),sQuery(id+"F2.wireOp",EDGE,"E27.bottom"),sQuery(id+"F2.wireOp",EDGE,"E27.right")])]});
            var Q1;
            Q1=makeQuery(id+"F5.opExtrude","SWEPT_EDGE",EDGE,{"disambiguationData":[OSD([sQuery(id+"F0.wireOp",EDGE,"E0.bottom"),sQuery(id+"F0.wireOp",EDGE,"E0.right")])]});
            var Q2;
            Q2=makeQuery(id+"F1.opExtrude","SWEPT_EDGE",EDGE,{"disambiguationData":[OSD([sQuery(id+"F0.wireOp",EDGE,"E0.bottom"),sQuery(id+"F0.wireOp",EDGE,"E0.right")])]});
            chamfer(context, id + "F9", {"entities" : qUnion([Q0, Q1, Q2]), "width" : 5 * mm, "tangentPropagation" : true});
        }
        {
            var Q0;
            Q0=makeQuery(id+"F1.opExtrude","CAP_FACE",FACE,{"disambiguationData":[OSD([sQuery(id+"F0.wireOp",EDGE,"E0.bottom"),sQuery(id+"F0.wireOp",EDGE,"E0.top"),sQuery(id+"F0.wireOp",EDGE,"E0.left"),sQuery(id+"F0.wireOp",EDGE,"E0.right"),sQuery(id+"F0.wireOp",EDGE,"E3"),sQuery(id+"F0.wireOp",EDGE,"E4"),sQuery(id+"F0.wireOp",EDGE,"E5"),sQuery(id+"F0.wireOp",EDGE,"E6"),sQuery(id+"F0.wireOp",EDGE,"E7"),sQuery(id+"F0.wireOp",EDGE,"E8"),sQuery(id+"F0.wireOp",EDGE,"E9.MirrorC"),sQuery(id+"F0.wireOp",EDGE,"E10.MirrorC"),sQuery(id+"F0.wireOp",EDGE,"E11.MirrorC"),sQuery(id+"F0.wireOp",EDGE,"E12.MirrorC"),sQuery(id+"F0.wireOp",EDGE,"E13.MirrorC"),sQuery(id+"F0.wireOp",EDGE,"E14.MirrorC"),sQuery(id+"F0.wireOp",EDGE,"E15.MirrorC"),sQuery(id+"F0.wireOp",EDGE,"E16.MirrorC"),sQuery(id+"F0.wireOp",EDGE,"E17.MirrorC"),sQuery(id+"F0.wireOp",EDGE,"E18.MirrorC"),sQuery(id+"F0.wireOp",EDGE,"E19.MirrorC"),sQuery(id+"F0.wireOp",EDGE,"E20.MirrorC"),sQuery(id+"F0.wireOp",EDGE,"E21.MirrorC"),sQuery(id+"F0.wireOp",EDGE,"E22.MirrorC"),sQuery(id+"F0.wireOp",EDGE,"E23.MirrorC"),sQuery(id+"F0.wireOp",EDGE,"E24.MirrorC"),sQuery(id+"F0.wireOp",EDGE,"E25.MirrorC"),sQuery(id+"F0.wireOp",EDGE,"E26.MirrorC")])],"isStart":false});
            var sketch = newSketch(context, id + "F10", { "sketchPlane" : qUnion([Q0])});
            skText(sketch, "E40", { "text": "HEPIA Epithelix V3", "fontName": "AllertaStencil-Regular.ttf"});
            const initialGuessF10  = {"E40": [0.06088, -0.02, 0, 1, 0.0031]};
            skSetInitialGuess(sketch, initialGuessF10);
            skSolve(sketch);
        }
        {
            var Q0;
            Q0 = qSketchRegion(id + "F10", true);
            extrude(context, id + "F11", {"entities" : qUnion([Q0]), "operationType" : NewBodyOperationType.REMOVE, "oppositeDirection" : true, "depth" : 0.1 * mm, "offsetDistance" : 25 * mm});
        }
    });
